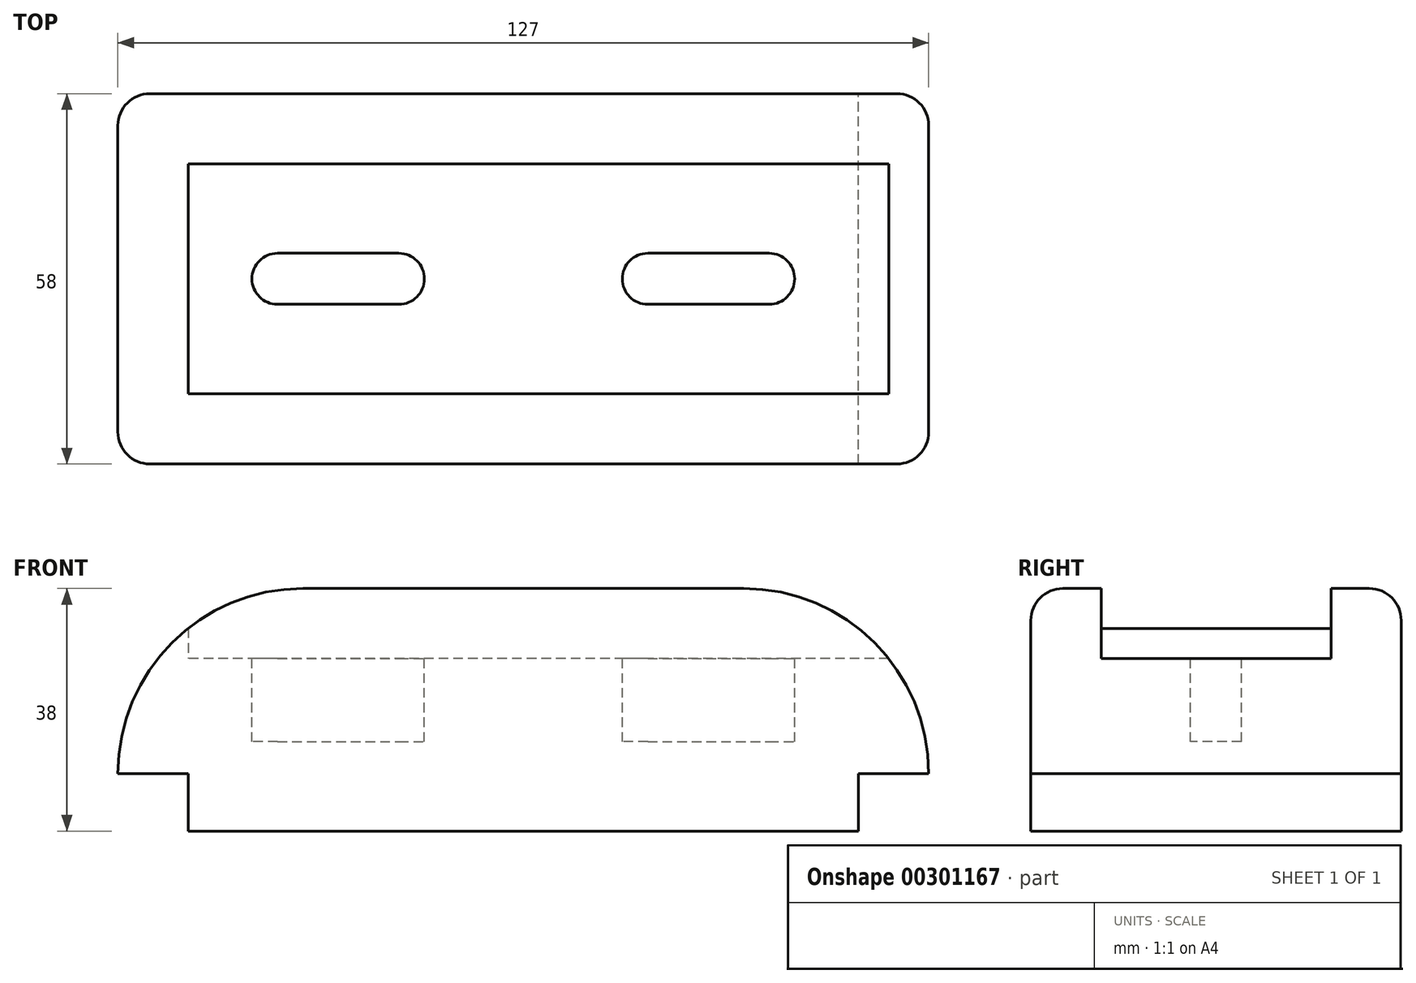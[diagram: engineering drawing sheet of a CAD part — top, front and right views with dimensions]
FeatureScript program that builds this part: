
annotation { "Feature Type Name" : "Feature", "Feature Type Description" : "" }
export const myFeature = defineFeature(function(context is Context, id is Id, definition is map)
    precondition{}
    {
        {
            var Q0;
            Q0=qCreatedBy(makeId("Front.planeOp"),FACE);
            var sketch = newSketch(context, id + "F0", { "sketchPlane" : qUnion([Q0])});
            skLineSegment(sketch, "E0", {"start": v(0, 0) * mm, "end": v(0, 9) * mm});
            skLineSegment(sketch, "E1", {"start": v(0, 9) * mm, "end": v(-11, 9) * mm});
            skLineSegment(sketch, "E2", {"start": v(0, 0) * mm, "end": v(105, 0) * mm});
            skLineSegment(sketch, "E3", {"start": v(105, 0) * mm, "end": v(105, 9) * mm});
            skLineSegment(sketch, "E4", {"start": v(105, 9) * mm, "end": v(116, 9) * mm});
            skArc(sketch, "E5", {"start": v(18, 38) * mm, "mid": v(-2.5, 29.5) * mm, "end": v(-11, 9) * mm});
            skLineSegment(sketch, "E6", {"start": v(18, 38) * mm, "end": v(87, 38) * mm});
            skArc(sketch, "E7", {"start": v(116, 9) * mm, "mid": v(107.5, 29.5) * mm, "end": v(87, 38) * mm});
            skSolve(sketch);
        }
        {
            var Q0;
            Q0=makeQuery(id+"F0.imprint","IMPRINT",FACE,{"disambiguationData":[TD([[makeQuery(id+"F0.imprint","IMPRINT",EDGE,{"derivedFrom":sQuery(id+"F0.wireOp",EDGE,"E0")}),-1.0]])]});
            extrude(context, id + "F1", {"entities" : qUnion([Q0]), "depth" : 58 * mm});
        }
        {
            var Q0;
            Q0=qCreatedBy(makeId("Right.planeOp"),FACE);
            var sketch = newSketch(context, id + "F2", { "sketchPlane" : qUnion([Q0])});
            skLineSegment(sketch, "E8.bottom", {"start": v(-47, 38) * mm, "end": v(-11, 38) * mm});
            skLineSegment(sketch, "E8.top", {"start": v(-47, 27) * mm, "end": v(-11, 27) * mm});
            skLineSegment(sketch, "E8.left", {"start": v(-47, 38) * mm, "end": v(-47, 27) * mm});
            skLineSegment(sketch, "E8.right", {"start": v(-11, 38) * mm, "end": v(-11, 27) * mm});
            skLineSegment(sketch, "E9.0.0", {"start": v(0, 9) * mm, "end": v(0, 38) * mm});
            skLineSegment(sketch, "E9.0.1", {"start": v(0, 38) * mm, "end": v(-58, 38) * mm});
            skLineSegment(sketch, "E9.0.2", {"start": v(-58, 38) * mm, "end": v(-58, 9) * mm});
            skLineSegment(sketch, "E9.0.3", {"start": v(-58, 9) * mm, "end": v(0, 9) * mm});
            skSolve(sketch);
        }
        {
            var Q0;
            Q0=makeQuery(id+"F2.imprint","IMPRINT",FACE,{"disambiguationData":[TD([[makeQuery(id+"F2.imprint","IMPRINT",EDGE,{"derivedFrom":sQuery(id+"F2.wireOp",EDGE,"E8.top")}),1.0]])]});
            extrude(context, id + "F3", {"entities" : qUnion([Q0]), "operationType" : NewBodyOperationType.REMOVE, "endBound" : BoundingType.THROUGH_ALL, "depth" : 25 * mm});
        }
        {
            var Q0;
            Q0=makeQuery(id+"F3.boolean.opBoolean","COPY",FACE,{"derivedFrom":makeQuery(id+"F3.opExtrude","SWEPT_FACE",FACE,{"disambiguationData":[OSD([sQuery(id+"F2.wireOp",EDGE,"E8.top")])]})});
            var sketch = newSketch(context, id + "F4", { "sketchPlane" : qUnion([Q0])});
            skLineSegment(sketch, "E10.bottom", {"start": v(14, -25) * mm, "end": v(33, -25) * mm});
            skLineSegment(sketch, "E10.top", {"start": v(14, -33) * mm, "end": v(33, -33) * mm});
            skLineSegment(sketch, "E11.bottom", {"start": v(72, -25) * mm, "end": v(91, -25) * mm});
            skLineSegment(sketch, "E11.top", {"start": v(72, -33) * mm, "end": v(91, -33) * mm});
            skArc(sketch, "E12", {"start": v(14, -25) * mm, "mid": v(10, -29) * mm, "end": v(14, -33) * mm});
            skArc(sketch, "E13", {"start": v(72, -25) * mm, "mid": v(68, -29) * mm, "end": v(72, -33) * mm});
            skArc(sketch, "E14", {"start": v(91, -33) * mm, "mid": v(95, -29) * mm, "end": v(91, -25) * mm});
            skArc(sketch, "E15", {"start": v(33, -33) * mm, "mid": v(37, -29) * mm, "end": v(33, -25) * mm});
            skSolve(sketch);
        }
        {
            var Q0;
            Q0=makeQuery(id+"F4.imprint","IMPRINT",FACE,{"disambiguationData":[TD([[makeQuery(id+"F4.imprint","IMPRINT",EDGE,{"derivedFrom":sQuery(id+"F4.wireOp",EDGE,"E11.bottom")}),-1.0]])]});
            var Q1;
            Q1=makeQuery(id+"F4.imprint","IMPRINT",FACE,{"disambiguationData":[TD([[makeQuery(id+"F4.imprint","IMPRINT",EDGE,{"derivedFrom":sQuery(id+"F4.wireOp",EDGE,"E10.bottom")}),-1.0]])]});
            extrude(context, id + "F5", {"entities" : qUnion([Q0, Q1]), "operationType" : NewBodyOperationType.REMOVE, "oppositeDirection" : true, "depth" : 13 * mm});
        }
        {
            var Q0;
            Q0=makeQuery(id+"F1.opExtrude","CAP_EDGE",EDGE,{"disambiguationData":[OSD([sQuery(id+"F0.wireOp",EDGE,"E5")])],"isStart":false});
            var Q1;
            Q1=makeQuery(id+"F1.opExtrude","CAP_EDGE",EDGE,{"disambiguationData":[OSD([sQuery(id+"F0.wireOp",EDGE,"E6")])],"isStart":false});
            var Q2;
            Q2=makeQuery(id+"F1.opExtrude","CAP_EDGE",EDGE,{"disambiguationData":[OSD([sQuery(id+"F0.wireOp",EDGE,"E7")])],"isStart":false});
            var Q3;
            Q3=makeQuery(id+"F1.opExtrude","CAP_EDGE",EDGE,{"disambiguationData":[OSD([sQuery(id+"F0.wireOp",EDGE,"E7")])],"isStart":true});
            var Q4;
            Q4=makeQuery(id+"F1.opExtrude","CAP_EDGE",EDGE,{"disambiguationData":[OSD([sQuery(id+"F0.wireOp",EDGE,"E6")])],"isStart":true});
            var Q5;
            Q5=makeQuery(id+"F1.opExtrude","CAP_EDGE",EDGE,{"disambiguationData":[OSD([sQuery(id+"F0.wireOp",EDGE,"E5")])],"isStart":true});
            fillet(context, id + "F6", {"entities" : qUnion([Q0, Q1, Q2, Q3, Q4, Q5]), "radius" : 5 * mm, "tangentPropagation" : true, "allowEdgeOverflow" : false});
        }
    });
